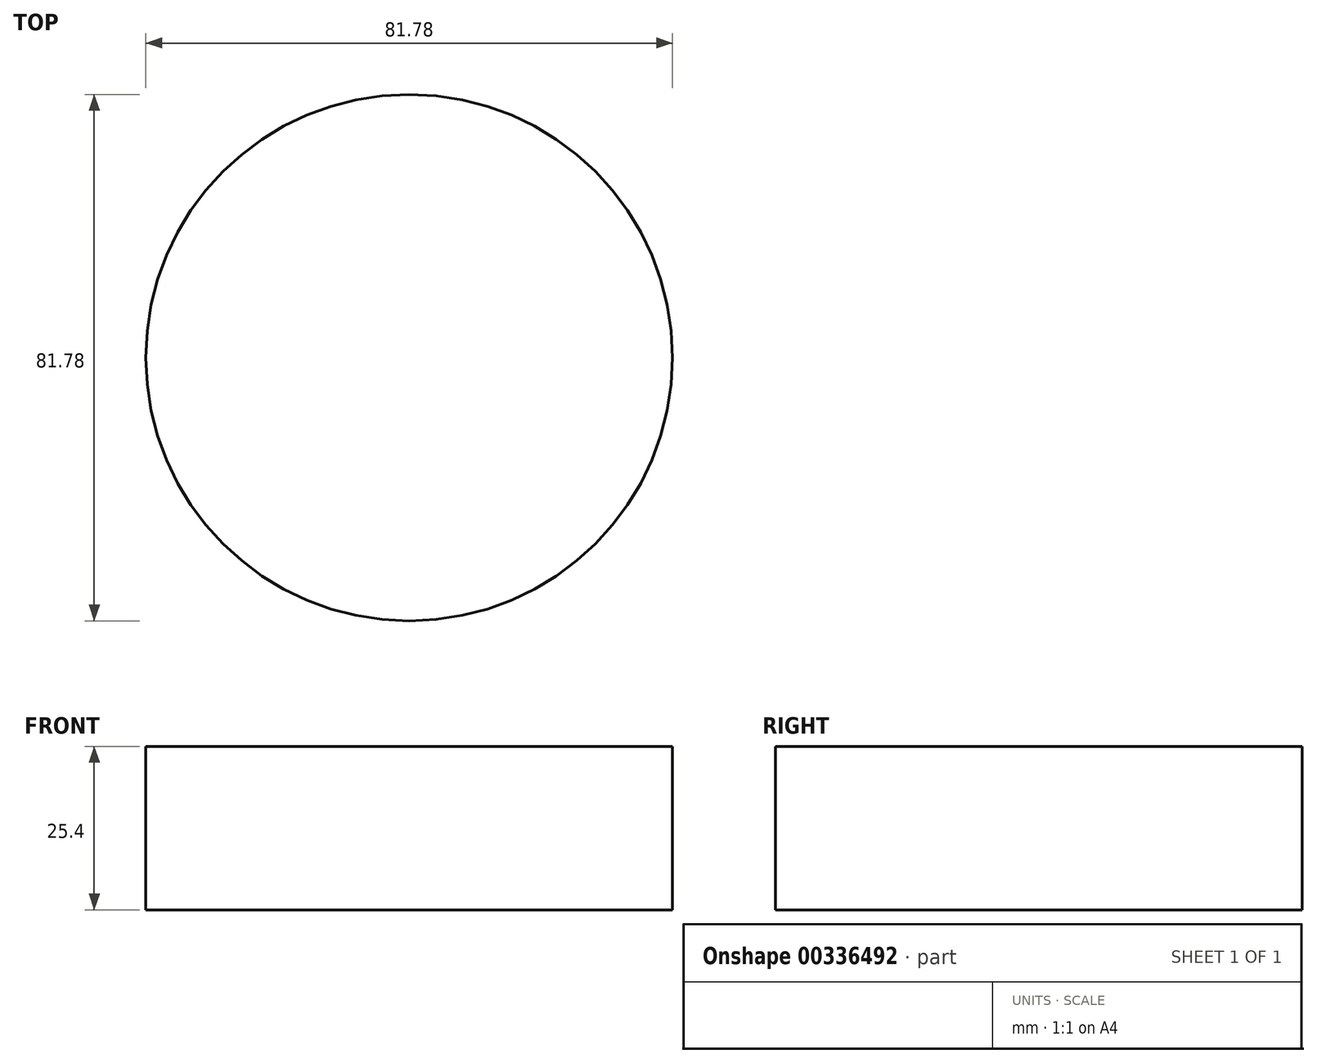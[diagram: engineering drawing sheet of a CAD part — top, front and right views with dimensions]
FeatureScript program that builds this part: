
annotation { "Feature Type Name" : "Feature", "Feature Type Description" : "" }
export const myFeature = defineFeature(function(context is Context, id is Id, definition is map)
    precondition{}
    {
        {
            var Q0;
            Q0=qCreatedBy(makeId("Top.planeOp"),FACE);
            var sketch = newSketch(context, id + "F0", { "sketchPlane" : qUnion([Q0])});
            skCircle(sketch, "E0", {"center": v(0, 0) * mm, "radius": 40.9 * mm});
            skSolve(sketch);
        }
        {
            var Q0;
            Q0 = qSketchRegion(id + "F0", true);
            extrude(context, id + "F1", {"entities" : qUnion([Q0]), "depth" : 25.4 * mm});
        }
    });
